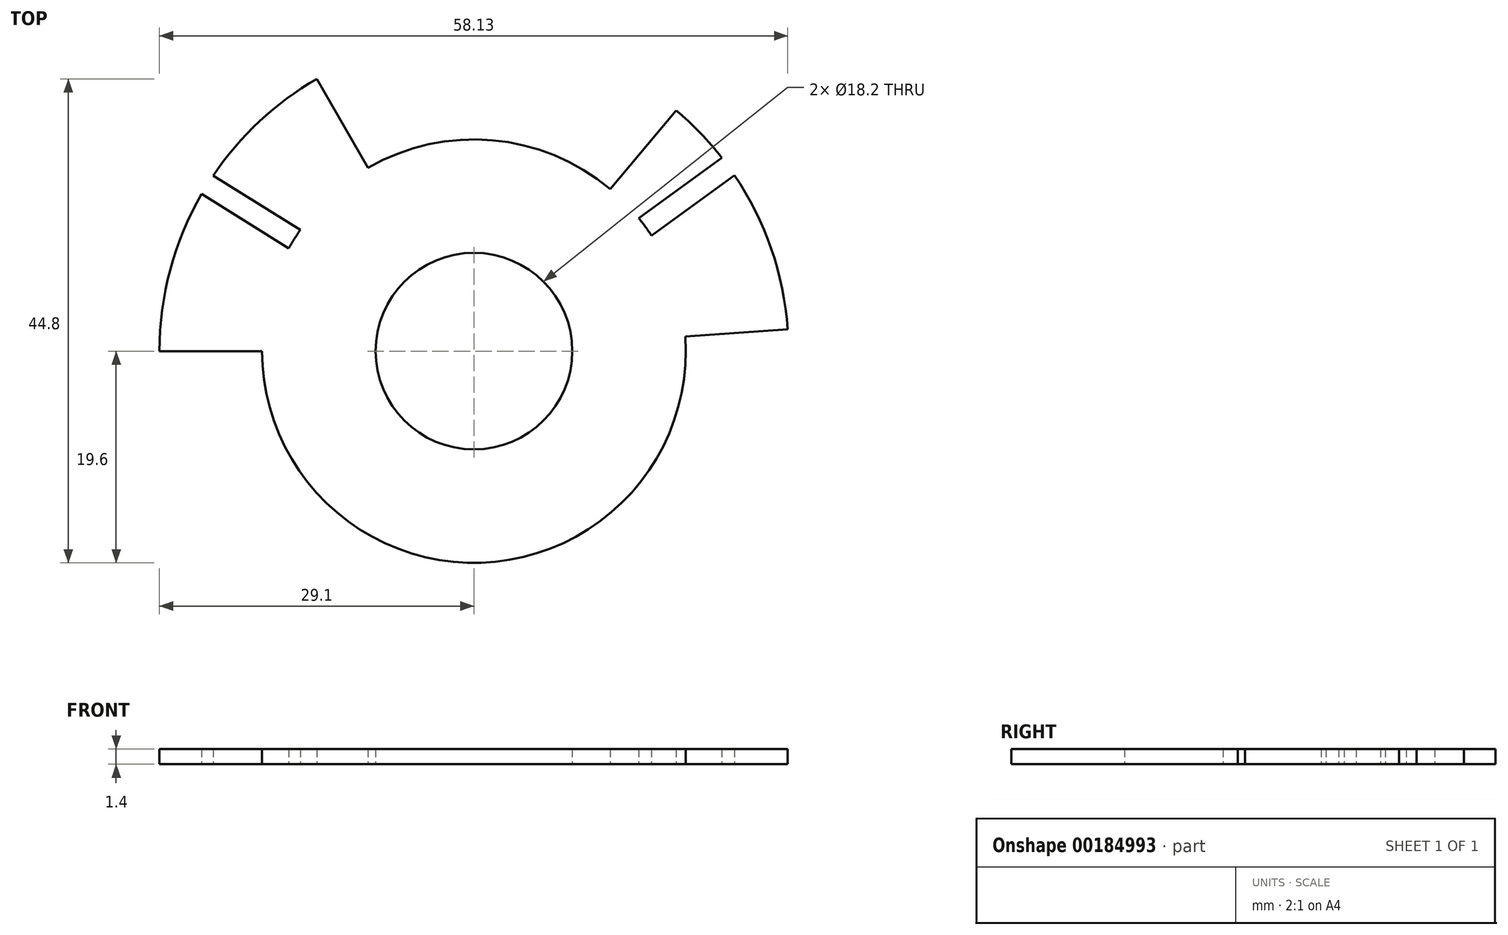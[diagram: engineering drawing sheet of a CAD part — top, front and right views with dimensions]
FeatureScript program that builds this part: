
annotation { "Feature Type Name" : "Feature", "Feature Type Description" : "" }
export const myFeature = defineFeature(function(context is Context, id is Id, definition is map)
    precondition{}
    {
        {
            var Q0;
            Q0=qCreatedBy(makeId("Top.planeOp"),FACE);
            var sketch = newSketch(context, id + "F0", { "sketchPlane" : qUnion([Q0])});
            skCircle(sketch, "E0", {"center": v(0, 0) * mm, "radius": 19.6 * mm});
            skCircle(sketch, "E1", {"center": v(0, 0) * mm, "radius": 9.1 * mm});
            skLineSegment(sketch, "E2", {"start": v(0, 0) * mm, "end": v(-19.6, 0) * mm});
            skLineSegment(sketch, "E3", {"start": v(0, 0) * mm, "end": v(19.6, 0) * mm});
            skLineSegment(sketch, "E4", {"start": v(0, 0) * mm, "end": v(-9.8, 16.97) * mm});
            skLineSegment(sketch, "E5", {"start": v(0, 0) * mm, "end": v(12.6, 15.01) * mm});
            skArc(sketch, "E6", {"start": v(21, 0) * mm, "mid": v(19.03, 8.87) * mm, "end": v(13.5, 16.09) * mm});
            skLineSegment(sketch, "E7", {"start": v(12.6, 15.01) * mm, "end": v(13.5, 16.09) * mm});
            skLineSegment(sketch, "E8", {"start": v(19.6, 0) * mm, "end": v(21, 0) * mm});
            skLineSegment(sketch, "E9", {"start": v(-9.8, 16.97) * mm, "end": v(-10.5, 18.19) * mm});
            skLineSegment(sketch, "E10", {"start": v(-19.6, 0) * mm, "end": v(-21, 0) * mm});
            skArc(sketch, "E11.trimOffspring", {"start": v(-10.5, 18.19) * mm, "mid": v(-18.19, 10.5) * mm, "end": v(-21, 0) * mm});
            skCircle(sketch, "E12", {"center": v(0, 0) * mm, "radius": 29.1 * mm});
            skLineSegment(sketch, "E13", {"start": v(13.5, 16.09) * mm, "end": v(18.7, 22.3) * mm});
            skLineSegment(sketch, "E14", {"start": v(21, 0) * mm, "end": v(29.1, 0) * mm});
            skLineSegment(sketch, "E15", {"start": v(-21, 0) * mm, "end": v(-29.1, 0) * mm});
            skLineSegment(sketch, "E16", {"start": v(-10.5, 18.19) * mm, "end": v(-14.55, 25.2) * mm});
            skLineSegment(sketch, "E17", {"start": v(0, 0) * mm, "end": v(-24.68, 15.42) * mm});
            skLineSegment(sketch, "E18", {"start": v(0, 0) * mm, "end": v(23.54, 17.1) * mm});
            skLineSegment(sketch, "E19.0", {"start": v(0.59, -0.8) * mm, "end": v(24.12, 16.29) * mm});
            skLineSegment(sketch, "E20.0", {"start": v(-0.59, 0.8) * mm, "end": v(22.94, 17.9) * mm});
            skLineSegment(sketch, "E21.0", {"start": v(0.53, 0.85) * mm, "end": v(-24.13, 16.26) * mm});
            skLineSegment(sketch, "E22.0", {"start": v(-0.53, -0.85) * mm, "end": v(-25.2, 14.56) * mm});
            skLineSegment(sketch, "E23", {"start": v(0, 0) * mm, "end": v(19.55, 1.37) * mm});
            skLineSegment(sketch, "E24", {"start": v(19.55, 1.37) * mm, "end": v(29.03, 2.03) * mm});
            skSolve(sketch);
        }
        {
            var Q0;
            {var subQ3=sQuery(id+"F0.wireOp",EDGE,"E23");var subQ5=sQuery(id+"F0.wireOp",EDGE,"E1");var subQ6=makeQuery(id+"F0.imprint","INTERSECT",VERTEX,{"derivedFrom":[subQ5,subQ3]});Q0=makeQuery(id+"F0.imprint","IMPRINT",FACE,{"disambiguationData":[TD([[makeQuery(id+"F0.imprint","IMPRINT",EDGE,{"disambiguationData":[TD([[subQ6,1.0]])],"derivedFrom":subQ5}),-1.0]])]});}
            var Q1;
            {var subQ0=sQuery(id+"F0.wireOp",EDGE,"E23");var subQ1=sQuery(id+"F0.wireOp",EDGE,"E0");var subQ2=makeQuery(id+"F0.imprint","INTERSECT",VERTEX,{"derivedFrom":[subQ1,subQ0]});Q1=makeQuery(id+"F0.imprint","IMPRINT",FACE,{"disambiguationData":[TD([[makeQuery(id+"F0.imprint","IMPRINT",EDGE,{"disambiguationData":[TD([[subQ2,-1.0]])],"derivedFrom":subQ1}),1.0]])]});}
            var Q2;
            {var subQ3=sQuery(id+"F0.wireOp",EDGE,"E20.0");var subQ5=sQuery(id+"F0.wireOp",EDGE,"E1");var subQ7=makeQuery(id+"F0.imprint","INTERSECT",VERTEX,{"derivedFrom":[subQ5,subQ3]});Q2=makeQuery(id+"F0.imprint","IMPRINT",FACE,{"disambiguationData":[TD([[makeQuery(id+"F0.imprint","IMPRINT",EDGE,{"disambiguationData":[TD([[subQ7,-1.0]])],"derivedFrom":subQ5}),-1.0]])]});}
            var Q3;
            {var subQ3=sQuery(id+"F0.wireOp",EDGE,"E5");var subQ5=sQuery(id+"F0.wireOp",EDGE,"E1");var subQ6=makeQuery(id+"F0.imprint","INTERSECT",VERTEX,{"derivedFrom":[subQ5,subQ3]});Q3=makeQuery(id+"F0.imprint","IMPRINT",FACE,{"disambiguationData":[TD([[makeQuery(id+"F0.imprint","IMPRINT",EDGE,{"disambiguationData":[TD([[subQ6,-1.0]])],"derivedFrom":subQ5}),-1.0]])]});}
            var Q4;
            {var subQ0=sQuery(id+"F0.wireOp",EDGE,"E4");var subQ5=sQuery(id+"F0.wireOp",EDGE,"E1");var subQ7=makeQuery(id+"F0.imprint","INTERSECT",VERTEX,{"derivedFrom":[subQ5,subQ0]});Q4=makeQuery(id+"F0.imprint","IMPRINT",FACE,{"disambiguationData":[TD([[makeQuery(id+"F0.imprint","IMPRINT",EDGE,{"disambiguationData":[TD([[subQ7,-1.0]])],"derivedFrom":subQ5}),-1.0]])]});}
            var Q5;
            {var subQ0=sQuery(id+"F0.wireOp",EDGE,"E21.0");var subQ1=sQuery(id+"F0.wireOp",EDGE,"E0");var subQ2=makeQuery(id+"F0.imprint","INTERSECT",VERTEX,{"derivedFrom":[subQ1,subQ0]});Q5=makeQuery(id+"F0.imprint","IMPRINT",FACE,{"disambiguationData":[TD([[makeQuery(id+"F0.imprint","IMPRINT",EDGE,{"disambiguationData":[TD([[subQ2,-1.0]])],"derivedFrom":subQ1}),1.0]])]});}
            var Q6;
            {var subQ0=sQuery(id+"F0.wireOp",EDGE,"E17");var subQ1=sQuery(id+"F0.wireOp",EDGE,"E0");var subQ2=makeQuery(id+"F0.imprint","INTERSECT",VERTEX,{"derivedFrom":[subQ1,subQ0]});Q6=makeQuery(id+"F0.imprint","IMPRINT",FACE,{"disambiguationData":[TD([[makeQuery(id+"F0.imprint","IMPRINT",EDGE,{"disambiguationData":[TD([[subQ2,-1.0]])],"derivedFrom":subQ1}),1.0]])]});}
            var Q7;
            {var subQ0=sQuery(id+"F0.wireOp",EDGE,"0SMqaixn-IP4D-q16D-n3Tg-mqc5c3AIDfgR");var subQ1=sQuery(id+"F0.wireOp",EDGE,"E0");var subQ2=makeQuery(id+"F0.imprint","INTERSECT",VERTEX,{"derivedFrom":[subQ1,subQ0]});Q7=makeQuery(id+"F0.imprint","IMPRINT",FACE,{"disambiguationData":[TD([[makeQuery(id+"F0.imprint","IMPRINT",EDGE,{"disambiguationData":[TD([[subQ2,1.0]])],"derivedFrom":subQ1}),1.0]])]});}
            var Q8;
            {var subQ3=sQuery(id+"F0.wireOp",EDGE,"0SMqaixn-IP4D-q16D-n3Tg-mqc5c3AIDfgR");var subQ5=sQuery(id+"F0.wireOp",EDGE,"E1");var subQ7=makeQuery(id+"F0.imprint","INTERSECT",VERTEX,{"derivedFrom":[subQ5,subQ3]});Q8=makeQuery(id+"F0.imprint","IMPRINT",FACE,{"disambiguationData":[TD([[makeQuery(id+"F0.imprint","IMPRINT",EDGE,{"disambiguationData":[TD([[subQ7,-1.0]])],"derivedFrom":subQ5}),-1.0]])]});}
            var Q9;
            {var subQ3=sQuery(id+"F0.wireOp",EDGE,"E3");var subQ5=sQuery(id+"F0.wireOp",EDGE,"E1");var subQ7=makeQuery(id+"F0.imprint","INTERSECT",VERTEX,{"derivedFrom":[subQ5,subQ3]});Q9=makeQuery(id+"F0.imprint","IMPRINT",FACE,{"disambiguationData":[TD([[makeQuery(id+"F0.imprint","IMPRINT",EDGE,{"disambiguationData":[TD([[subQ7,1.0]])],"derivedFrom":subQ5}),-1.0]])]});}
            var Q10;
            {var subQ0=sQuery(id+"F0.wireOp",EDGE,"E7");Q10=makeQuery(id+"F0.imprint","IMPRINT",FACE,{"disambiguationData":[TD([[makeQuery(id+"F0.imprint","IMPRINT",EDGE,{"derivedFrom":subQ0}),-1.0]])]});}
            var Q11;
            {var subQ0=sQuery(id+"F0.wireOp",EDGE,"E13");Q11=makeQuery(id+"F0.imprint","IMPRINT",FACE,{"disambiguationData":[TD([[makeQuery(id+"F0.imprint","IMPRINT",EDGE,{"derivedFrom":subQ0}),-1.0]])]});}
            var Q12;
            {var subQ0=sQuery(id+"F0.wireOp",EDGE,"E9");Q12=makeQuery(id+"F0.imprint","IMPRINT",FACE,{"disambiguationData":[TD([[makeQuery(id+"F0.imprint","IMPRINT",EDGE,{"derivedFrom":subQ0}),1.0]])]});}
            var Q13;
            {var subQ1=sQuery(id+"F0.wireOp",EDGE,"E10");Q13=makeQuery(id+"F0.imprint","IMPRINT",FACE,{"disambiguationData":[TD([[makeQuery(id+"F0.imprint","IMPRINT",EDGE,{"derivedFrom":subQ1}),-1.0]])]});}
            var Q14;
            {var subQ0=sQuery(id+"F0.wireOp",EDGE,"E15");Q14=makeQuery(id+"F0.imprint","IMPRINT",FACE,{"disambiguationData":[TD([[makeQuery(id+"F0.imprint","IMPRINT",EDGE,{"derivedFrom":subQ0}),-1.0]])]});}
            var Q15;
            {var subQ0=sQuery(id+"F0.wireOp",EDGE,"E16");Q15=makeQuery(id+"F0.imprint","IMPRINT",FACE,{"disambiguationData":[TD([[makeQuery(id+"F0.imprint","IMPRINT",EDGE,{"derivedFrom":subQ0}),1.0]])]});}
            var Q16;
            {var subQ0=sQuery(id+"F0.wireOp",EDGE,"E18");var subQ1=sQuery(id+"F0.wireOp",EDGE,"E0");var subQ2=makeQuery(id+"F0.imprint","INTERSECT",VERTEX,{"derivedFrom":[subQ1,subQ0]});Q16=makeQuery(id+"F0.imprint","IMPRINT",FACE,{"disambiguationData":[TD([[makeQuery(id+"F0.imprint","IMPRINT",EDGE,{"disambiguationData":[TD([[subQ2,-1.0]])],"derivedFrom":subQ1}),1.0]])]});}
            var Q17;
            {var subQ0=sQuery(id+"F0.wireOp",EDGE,"E19.0");var subQ1=sQuery(id+"F0.wireOp",EDGE,"E0");var subQ2=makeQuery(id+"F0.imprint","INTERSECT",VERTEX,{"derivedFrom":[subQ1,subQ0]});Q17=makeQuery(id+"F0.imprint","IMPRINT",FACE,{"disambiguationData":[TD([[makeQuery(id+"F0.imprint","IMPRINT",EDGE,{"disambiguationData":[TD([[subQ2,-1.0]])],"derivedFrom":subQ1}),1.0]])]});}
            var Q18;
            {var subQ0=sQuery(id+"F0.wireOp",EDGE,"E24");var subQ1=sQuery(id+"F0.wireOp",EDGE,"E6");var subQ2=makeQuery(id+"F0.imprint","INTERSECT",VERTEX,{"derivedFrom":[subQ1,subQ0]});Q18=makeQuery(id+"F0.imprint","IMPRINT",FACE,{"disambiguationData":[TD([[makeQuery(id+"F0.imprint","IMPRINT",EDGE,{"disambiguationData":[TD([[subQ2,-1.0]])],"derivedFrom":subQ1}),-1.0]])]});}
            var Q19;
            {var subQ0=sQuery(id+"F0.wireOp",EDGE,"E24");var subQ5=sQuery(id+"F0.wireOp",EDGE,"E6");var subQ6=makeQuery(id+"F0.imprint","INTERSECT",VERTEX,{"derivedFrom":[subQ5,subQ0]});Q19=makeQuery(id+"F0.imprint","IMPRINT",FACE,{"disambiguationData":[TD([[makeQuery(id+"F0.imprint","IMPRINT",EDGE,{"disambiguationData":[TD([[subQ6,-1.0]])],"derivedFrom":subQ5}),1.0]])]});}
            extrude(context, id + "F1", {"entities" : qUnion([Q0, Q1, Q2, Q3, Q4, Q5, Q6, Q7, Q8, Q9, Q10, Q11, Q12, Q13, Q14, Q15, Q16, Q17, Q18, Q19]), "depth" : 1.4 * mm});
        }
    });
